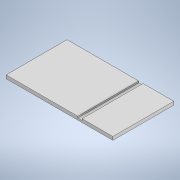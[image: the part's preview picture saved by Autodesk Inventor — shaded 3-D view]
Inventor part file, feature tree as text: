
AUTODESK INVENTOR PART (.ipt)
format: ipt  version: 2021.1 (Build 251245010, 245A)  size: 104,448 bytes
history: native  units: mm
features: extrude x2, sketch x2, other x1
ambient origin geometry x8: Origin, YZ Plane, XZ Plane, XY Plane, X Axis, Y Axis, Z Axis, Center Point
bodies: Body1 (feature_tree)
feature tree (5):
  other  "Твердое тело1"
  extrude  "Выдавливание1"  Depth=70.0mm
  extrude  "Выдавливание2"  Depth=40.0mm
  sketch  "Эскиз1"
  sketch  "Эскиз2"
